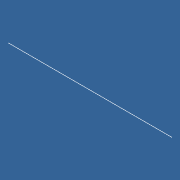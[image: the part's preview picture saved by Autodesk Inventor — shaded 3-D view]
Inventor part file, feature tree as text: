
AUTODESK INVENTOR PART (.ipt)
format: ipt  version: unknown  size: 160,256 bytes
history: native  units: in
note: dims shown in document units (in); Inventor stores cm internally (conversion verified against a paired STEP export)
features: extrude x1, sketch x1
ambient origin geometry x8: Origin, YZ Plane, XZ Plane, XY Plane, X Axis, Y Axis, Z Axis, Center Point
bodies: Solid1 (feature_tree)
feature tree (2):
  extrude  "Extrusion1"  Depth=648.0in
  sketch  "Sketch1"  dims[d0=2.0in d1=648.0in d2=0.06in d3=0.0in]
